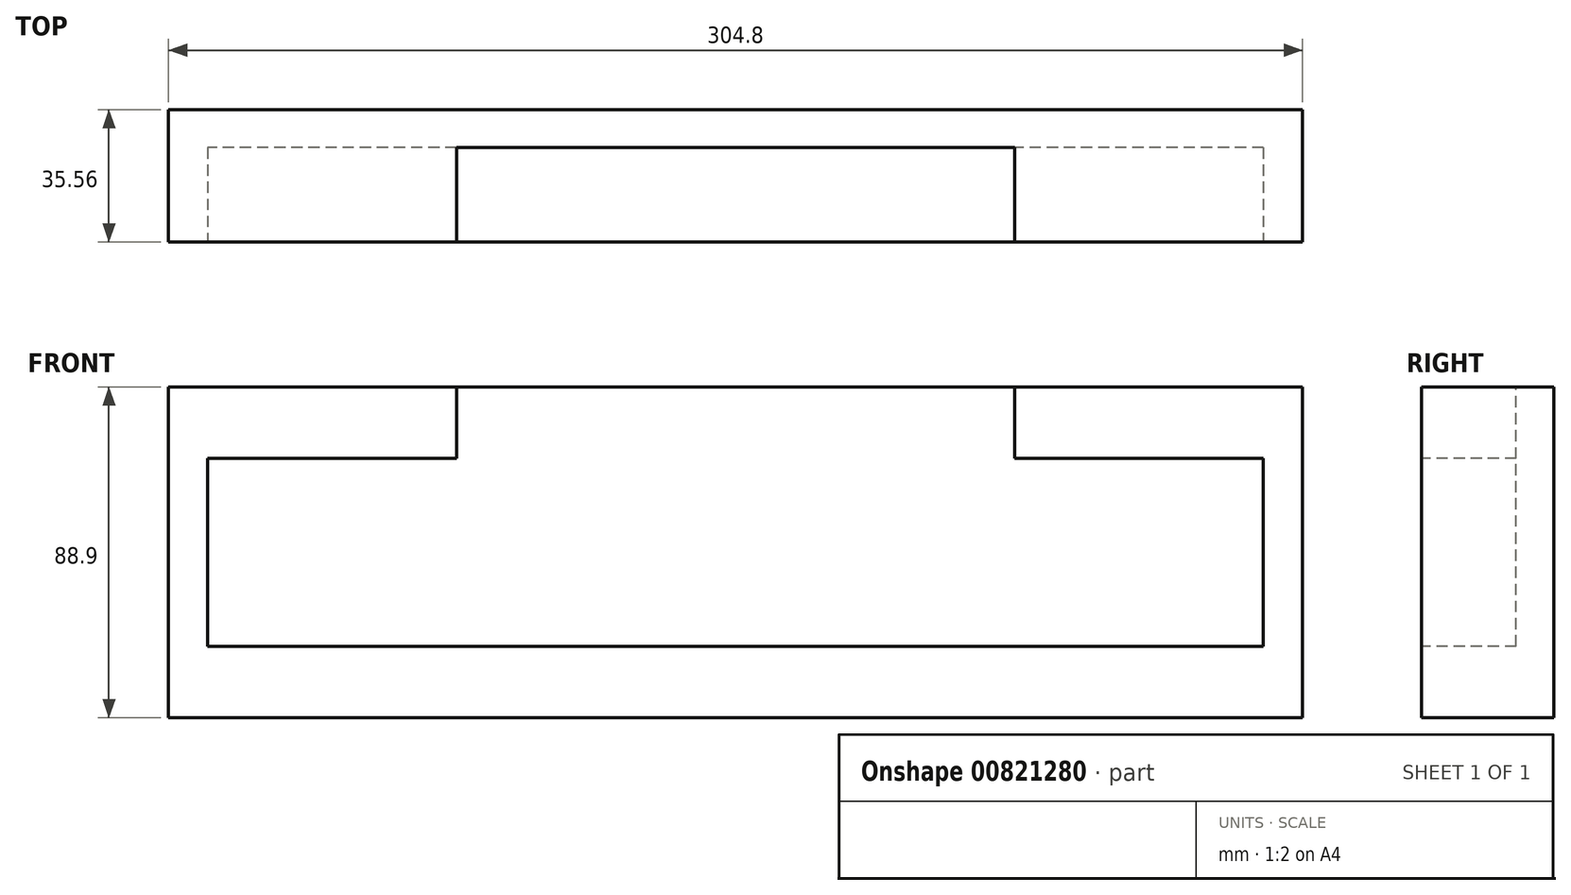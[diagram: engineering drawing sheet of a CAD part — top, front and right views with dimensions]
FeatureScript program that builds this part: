
annotation { "Feature Type Name" : "Feature", "Feature Type Description" : "" }
export const myFeature = defineFeature(function(context is Context, id is Id, definition is map)
    precondition{}
    {
        {
            var Q0;
            Q0=qCreatedBy(makeId("Front.planeOp"),FACE);
            var sketch = newSketch(context, id + "F0", { "sketchPlane" : qUnion([Q0])});
            skLineSegment(sketch, "E0.bottom", {"start": v(152.4, -44.45) * mm, "end": v(-152.4, -44.45) * mm});
            skLineSegment(sketch, "E0.top", {"start": v(152.4, 44.45) * mm, "end": v(-152.4, 44.45) * mm});
            skLineSegment(sketch, "E0.left", {"start": v(152.4, -44.45) * mm, "end": v(152.4, 44.45) * mm});
            skLineSegment(sketch, "E0.right", {"start": v(-152.4, -44.45) * mm, "end": v(-152.4, 44.45) * mm});
            skPoint(sketch, "E0.middle", {"position": v(0, 0) * mm});
            skSolve(sketch);
        }
        {
            var Q0;
            Q0=makeQuery(id+"F0.imprint","IMPRINT",FACE,{"disambiguationData":[TD([[makeQuery(id+"F0.imprint","IMPRINT",EDGE,{"derivedFrom":sQuery(id+"F0.wireOp",EDGE,"E0.bottom")}),-1.0]])]});
            extrude(context, id + "F1", {"entities" : qUnion([Q0]), "depth" : 35.56 * mm, "offsetDistance" : 25.4 * mm});
        }
        {
            var Q0;
            Q0=makeQuery(id+"F1.opExtrude","CAP_FACE",FACE,{"disambiguationData":[OSD([sQuery(id+"F0.wireOp",EDGE,"E0.bottom"),sQuery(id+"F0.wireOp",EDGE,"E0.top"),sQuery(id+"F0.wireOp",EDGE,"E0.left"),sQuery(id+"F0.wireOp",EDGE,"E0.right")])],"isStart":false});
            var sketch = newSketch(context, id + "F2", { "sketchPlane" : qUnion([Q0])});
            skLineSegment(sketch, "E1.bottom", {"start": v(-33.34, 44.45) * mm, "end": v(33.34, 44.45) * mm});
            skLineSegment(sketch, "E1.top", {"start": v(-33.34, 19.15) * mm, "end": v(33.34, 19.15) * mm});
            skLineSegment(sketch, "E1.left", {"start": v(-33.34, 44.45) * mm, "end": v(-33.34, 19.15) * mm});
            skLineSegment(sketch, "E1.right", {"start": v(33.34, 44.45) * mm, "end": v(33.34, 19.15) * mm});
            skPoint(sketch, "E1.middle", {"position": v(0, 31.8) * mm});
            skLineSegment(sketch, "E2.bottom", {"start": v(75, -25.25) * mm, "end": v(-75, -25.25) * mm});
            skLineSegment(sketch, "E2.top", {"start": v(75, 44.46) * mm, "end": v(-75, 44.46) * mm});
            skLineSegment(sketch, "E2.left", {"start": v(75, -25.25) * mm, "end": v(75, 44.46) * mm});
            skLineSegment(sketch, "E2.right", {"start": v(-75, -25.25) * mm, "end": v(-75, 44.46) * mm});
            skPoint(sketch, "E2.middle", {"position": v(0, 9.6) * mm});
            skLineSegment(sketch, "E3.bottom", {"start": v(75, -25.25) * mm, "end": v(141.86, -25.25) * mm});
            skLineSegment(sketch, "E3.top", {"start": v(75, 25.25) * mm, "end": v(141.86, 25.25) * mm});
            skLineSegment(sketch, "E3.left", {"start": v(75, -25.25) * mm, "end": v(75, 25.25) * mm});
            skLineSegment(sketch, "E3.right", {"start": v(141.86, -25.25) * mm, "end": v(141.86, 25.25) * mm});
            skPoint(sketch, "E3.middle", {"position": v(108.43, 0) * mm});
            skLineSegment(sketch, "E4.bottom", {"start": v(-75, -25.25) * mm, "end": v(-141.86, -25.25) * mm});
            skLineSegment(sketch, "E4.top", {"start": v(-75, 25.25) * mm, "end": v(-141.86, 25.25) * mm});
            skLineSegment(sketch, "E4.left", {"start": v(-75, -25.25) * mm, "end": v(-75, 25.25) * mm});
            skLineSegment(sketch, "E4.right", {"start": v(-141.86, -25.25) * mm, "end": v(-141.86, 25.25) * mm});
            skPoint(sketch, "E4.middle", {"position": v(-108.43, 0) * mm});
            skSolve(sketch);
        }
        {
            var Q0;
            {var subQ0=sQuery(id+"F2.wireOp",EDGE,"E2.left");var subQ1=sQuery(id+"F2.wireOp",EDGE,"kyOX0tx4-TR9g-jIeM-GMcn-RSNUBwiJVp1N");var subQ3=makeQuery(id+"F2.imprint","INTERSECT",VERTEX,{"derivedFrom":[subQ1,subQ0]});Q0=makeQuery(id+"F2.imprint","IMPRINT",FACE,{"disambiguationData":[TD([[makeQuery(id+"F2.imprint","IMPRINT",EDGE,{"disambiguationData":[TD([[subQ3,1.0]])],"derivedFrom":subQ1}),1.0]])]});}
            var Q1;
            {var subQ0=sQuery(id+"F2.wireOp",EDGE,"E2.left");var subQ1=sQuery(id+"F2.wireOp",EDGE,"kyOX0tx4-TR9g-jIeM-GMcn-RSNUBwiJVp1N");var subQ3=makeQuery(id+"F2.imprint","INTERSECT",VERTEX,{"derivedFrom":[subQ1,subQ0]});Q1=makeQuery(id+"F2.imprint","IMPRINT",FACE,{"disambiguationData":[TD([[makeQuery(id+"F2.imprint","IMPRINT",EDGE,{"disambiguationData":[TD([[subQ3,-1.0]])],"derivedFrom":subQ1}),1.0]])]});}
            var Q2;
            Q2=makeQuery(id+"F2.imprint","IMPRINT",FACE,{"disambiguationData":[TD([[makeQuery(id+"F2.imprint","IMPRINT",EDGE,{"derivedFrom":sQuery(id+"F2.wireOp",EDGE,"E1.top")}),-1.0]])]});
            var Q3;
            {var subQ0=sQuery(id+"F2.wireOp",EDGE,"E2.bottom");var subQ1=sQuery(id+"F2.wireOp",EDGE,"G8hMyFlK-JlFC-bd5F-lcb4-lyxPWgE1AGwx");var subQ2=makeQuery(id+"F2.imprint","INTERSECT",VERTEX,{"derivedFrom":[subQ1,subQ0]});Q3=makeQuery(id+"F2.imprint","IMPRINT",FACE,{"disambiguationData":[TD([[makeQuery(id+"F2.imprint","IMPRINT",EDGE,{"disambiguationData":[TD([[subQ2,1.0]])],"derivedFrom":subQ1}),1.0]])]});}
            var Q4;
            {var subQ0=sQuery(id+"F2.wireOp",EDGE,"E2.bottom");var subQ1=sQuery(id+"F2.wireOp",EDGE,"G8hMyFlK-JlFC-bd5F-lcb4-lyxPWgE1AGwx");var subQ2=makeQuery(id+"F2.imprint","INTERSECT",VERTEX,{"derivedFrom":[subQ1,subQ0]});Q4=makeQuery(id+"F2.imprint","IMPRINT",FACE,{"disambiguationData":[TD([[makeQuery(id+"F2.imprint","IMPRINT",EDGE,{"disambiguationData":[TD([[subQ2,-1.0]])],"derivedFrom":subQ1}),1.0]])]});}
            extrude(context, id + "F3", {"entities" : qUnion([Q0, Q1, Q2, Q3, Q4]), "operationType" : NewBodyOperationType.REMOVE, "oppositeDirection" : true, "depth" : 25.4 * mm, "offsetDistance" : 25.4 * mm});
        }
        {
            var Q0;
            {var subQ0=sQuery(id+"F0.wireOp",EDGE,"E0.top");Q0=makeQuery(id+"F3.boolean.opBoolean","SPLIT",FACE,{"disambiguationData":[TD([makeQuery(id+"F3.opExtrude","SWEPT_FACE",FACE,{"disambiguationData":[OSD([sQuery(id+"F2.wireOp",EDGE,"E1.top")])]})])],"derivedFrom":makeQuery(id+"F1.opExtrude","CAP_FACE",FACE,{"disambiguationData":[OSD([sQuery(id+"F0.wireOp",EDGE,"E0.bottom"),subQ0,sQuery(id+"F0.wireOp",EDGE,"E0.left"),sQuery(id+"F0.wireOp",EDGE,"E0.right")])],"isStart":false})});}
            extrude(context, id + "F4", {"entities" : qUnion([Q0]), "operationType" : NewBodyOperationType.REMOVE, "oppositeDirection" : true, "depth" : 25.4 * mm, "offsetDistance" : 25.4 * mm});
        }
        {
            var Q0;
            Q0=makeQuery(id+"F2.imprint","IMPRINT",FACE,{"disambiguationData":[TD([[makeQuery(id+"F2.imprint","IMPRINT",EDGE,{"derivedFrom":sQuery(id+"F2.wireOp",EDGE,"E4.bottom")}),-1.0]])]});
            var Q1;
            Q1=makeQuery(id+"F2.imprint","IMPRINT",FACE,{"disambiguationData":[TD([[makeQuery(id+"F2.imprint","IMPRINT",EDGE,{"derivedFrom":sQuery(id+"F2.wireOp",EDGE,"E3.bottom")}),1.0]])]});
            extrude(context, id + "F5", {"entities" : qUnion([Q0, Q1]), "operationType" : NewBodyOperationType.REMOVE, "oppositeDirection" : true, "depth" : 25.4 * mm, "offsetDistance" : 25.4 * mm});
        }
    });
